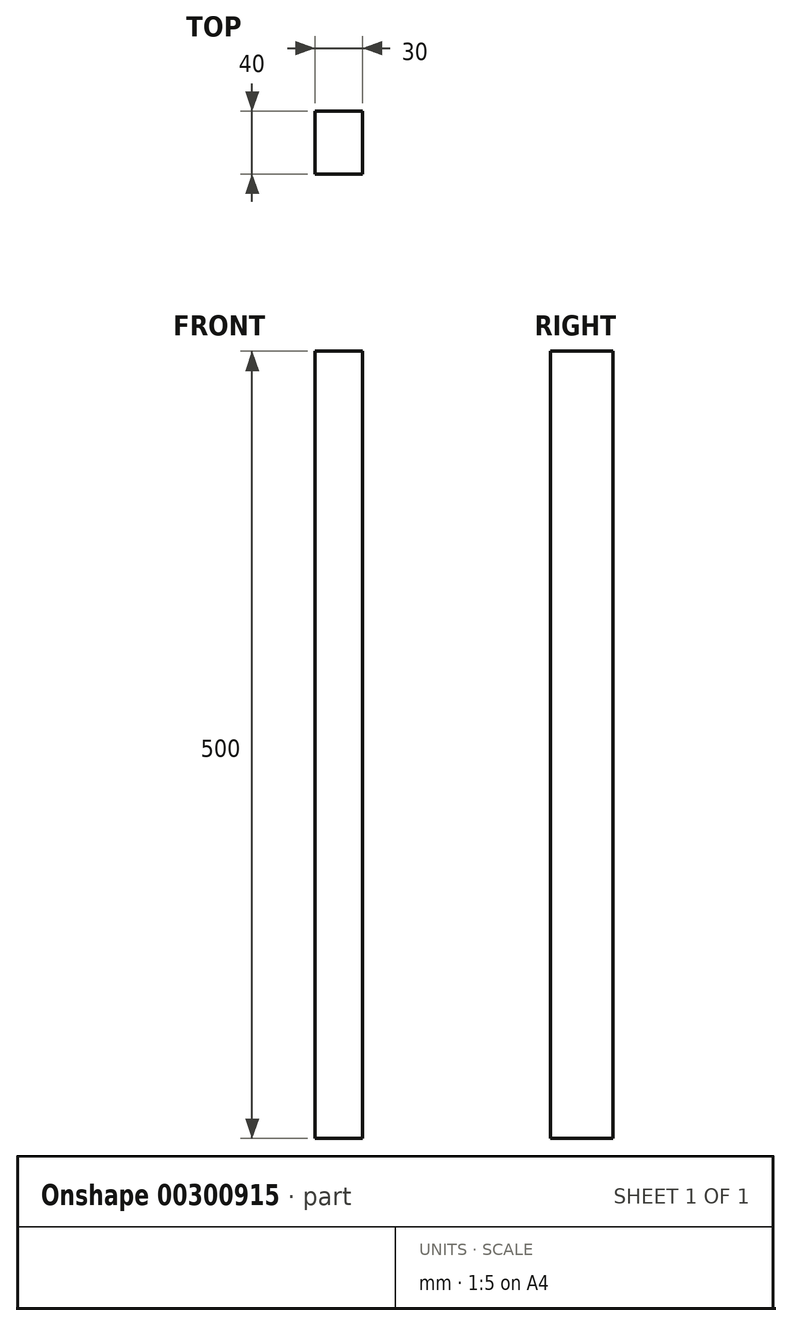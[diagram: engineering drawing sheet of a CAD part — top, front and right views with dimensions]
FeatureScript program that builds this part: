
annotation { "Feature Type Name" : "Feature", "Feature Type Description" : "" }
export const myFeature = defineFeature(function(context is Context, id is Id, definition is map)
    precondition{}
    {
        {
            var Q0;
            Q0=qCreatedBy(makeId("Front.planeOp"),FACE);
            var sketch = newSketch(context, id + "F0", { "sketchPlane" : qUnion([Q0])});
            skLineSegment(sketch, "E0.bottom", {"start": v(0, 0) * mm, "end": v(30, 0) * mm});
            skLineSegment(sketch, "E0.top", {"start": v(0, 500) * mm, "end": v(30, 500) * mm});
            skLineSegment(sketch, "E0.left", {"start": v(0, 0) * mm, "end": v(0, 500) * mm});
            skLineSegment(sketch, "E0.right", {"start": v(30, 0) * mm, "end": v(30, 500) * mm});
            skSolve(sketch);
        }
        {
            var Q0;
            Q0=makeQuery(id+"F0.imprint","IMPRINT",FACE,{"disambiguationData":[TD([[makeQuery(id+"F0.imprint","IMPRINT",EDGE,{"derivedFrom":sQuery(id+"F0.wireOp",EDGE,"E0.bottom")}),1.0]])]});
            extrude(context, id + "F1", {"entities" : qUnion([Q0]), "depth" : 40 * mm});
        }
    });
